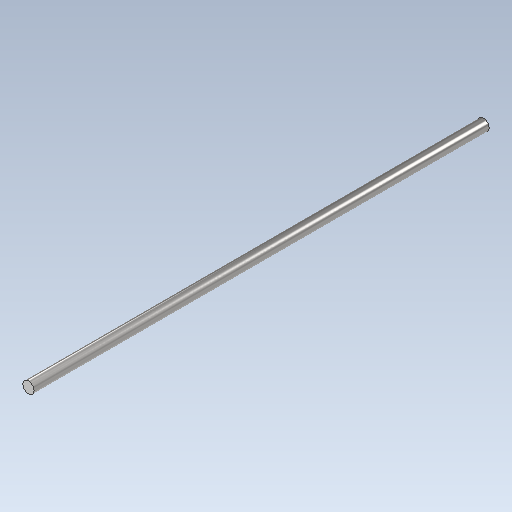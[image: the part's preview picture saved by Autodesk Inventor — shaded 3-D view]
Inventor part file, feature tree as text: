
AUTODESK INVENTOR PART (.ipt)
format: ipt  version: 2020 (Build 240168000, 168)  size: 92,672 bytes
history: native  units: mm
features: other x4, extrude x1, sketch x1, reference x1
ambient origin geometry x8: Origin, YZ Plane, XZ Plane, XY Plane, X Axis, Y Axis, Z Axis, Center Point
bodies: Body1 (feature_tree)
feature tree (7):
  other  "Bryła1"
  extrude  "Wyciągnięcie proste1"  Depth=100.0mm TaperAngle=0.0deg
  sketch  "Szkic1"
  reference  "Odniesienie1"
  other  "<userpath>\Desktop\3d\scanning-robot\Assembly1.iam"
  other  "Assembly1.iam"
  other  "wheel-adapter:1"
